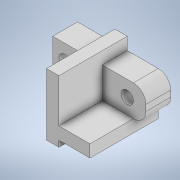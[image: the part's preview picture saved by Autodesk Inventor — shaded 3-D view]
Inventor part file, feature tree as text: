
AUTODESK INVENTOR PART (.ipt)
format: ipt  version: 2021 (Build 250183000, 183)  size: 152,064 bytes
history: native  units: mm
features: sketch x5, extrude x4, hole x1, fillet x1
ambient origin geometry x8: Origin, YZ Plane, XZ Plane, XY Plane, X Axis, Y Axis, Z Axis, Center Point
bodies: Solid1 (feature_tree)
feature tree (11):
  extrude  "Extrusion1"  Depth=5.0mm
  hole  "Hole1"  [1 undecoded]
  extrude  "Extrusion2"  Depth=2.0mm
  fillet  "Fillet1"  Radius=10.0mm
  extrude  "Extrusion3"  Depth=6.0mm
  extrude  "Extrusion4"  Depth=2.0mm
  sketch  "Sketch1"  dims[d0=15.0mm d1=5.0mm]
  sketch  "Sketch2"  dims[d2=4.0mm d3=0.0mm d4=2.5mm]
  sketch  "Sketch3"  dims[d5=2.5mm d6=2.0mm d7=10.0mm]
  sketch  "Sketch4"  dims[d8=2.0mm d9=6.0mm d10=4.0mm d11=2.0mm d12=90.0deg d13=4.0mm d14=20.594885mm d15=6.0mm]
  sketch  "Sketch5"  dims[d16=2.0mm d17=12.0mm d18=2.0mm d19=11.0mm d20=0.0mm d21=2.0mm d22=2.0mm d23=0.0mm d24=2.0mm d25=0.0mm]
note: 1 required parameter value undecoded (feature->parameter linkage not recoverable at this tier; creation-order binding heuristic only, values carry confidence <= 0.55)
